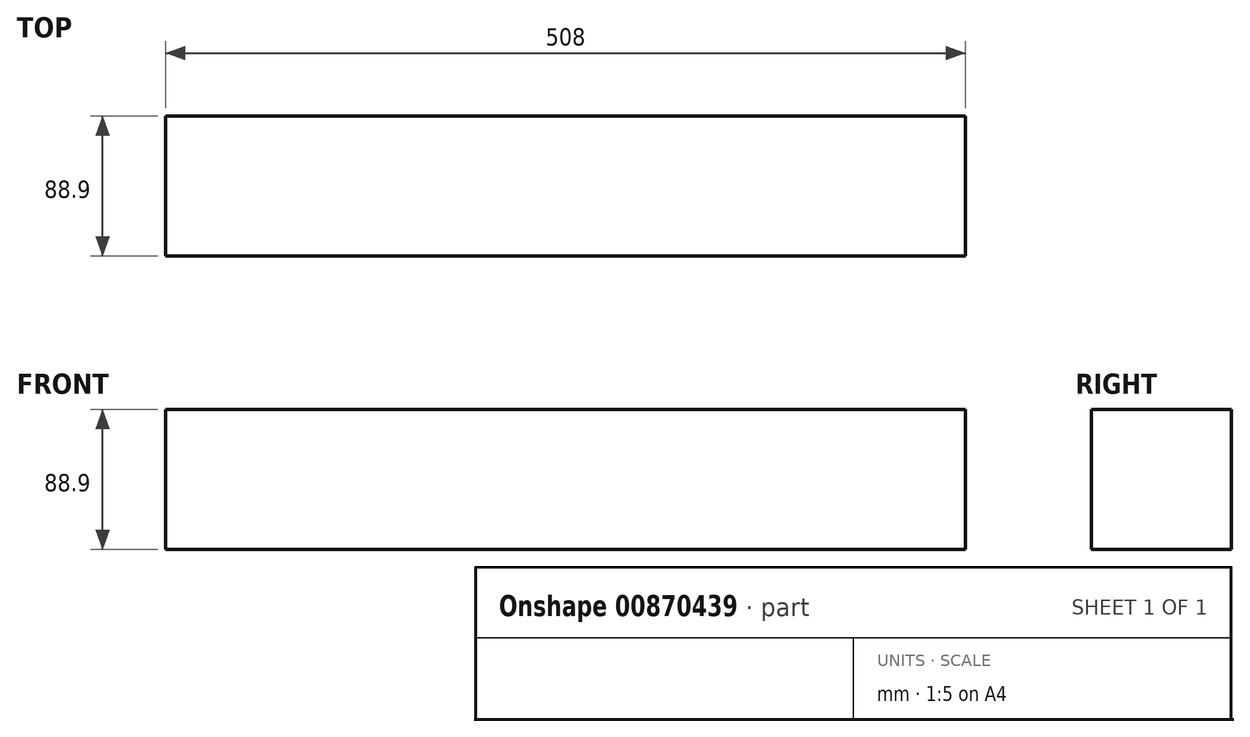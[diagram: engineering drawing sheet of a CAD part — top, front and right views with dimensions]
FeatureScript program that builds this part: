
annotation { "Feature Type Name" : "Feature", "Feature Type Description" : "" }
export const myFeature = defineFeature(function(context is Context, id is Id, definition is map)
    precondition{}
    {
        {
            var Q0;
            Q0=qCreatedBy(makeId("Right.planeOp"),FACE);
            var sketch = newSketch(context, id + "F0", { "sketchPlane" : qUnion([Q0])});
            skLineSegment(sketch, "E0.bottom", {"start": v(46.26, 44.45) * mm, "end": v(-42.64, 44.45) * mm});
            skLineSegment(sketch, "E0.top", {"start": v(46.26, -44.45) * mm, "end": v(-42.64, -44.45) * mm});
            skLineSegment(sketch, "E0.left", {"start": v(46.26, 44.45) * mm, "end": v(46.26, -44.45) * mm});
            skLineSegment(sketch, "E0.right", {"start": v(-42.64, 44.45) * mm, "end": v(-42.64, -44.45) * mm});
            skPoint(sketch, "E0.middle", {"position": v(1.8, 0) * mm});
            skSolve(sketch);
        }
        {
            var Q0;
            Q0=makeQuery(id+"F0.imprint","IMPRINT",FACE,{"disambiguationData":[TD([[makeQuery(id+"F0.imprint","IMPRINT",EDGE,{"derivedFrom":sQuery(id+"F0.wireOp",EDGE,"E0.bottom")}),1.0]])]});
            extrude(context, id + "F1", {"entities" : qUnion([Q0]), "depth" : 508 * mm, "offsetDistance" : 25.4 * mm});
        }
    });
